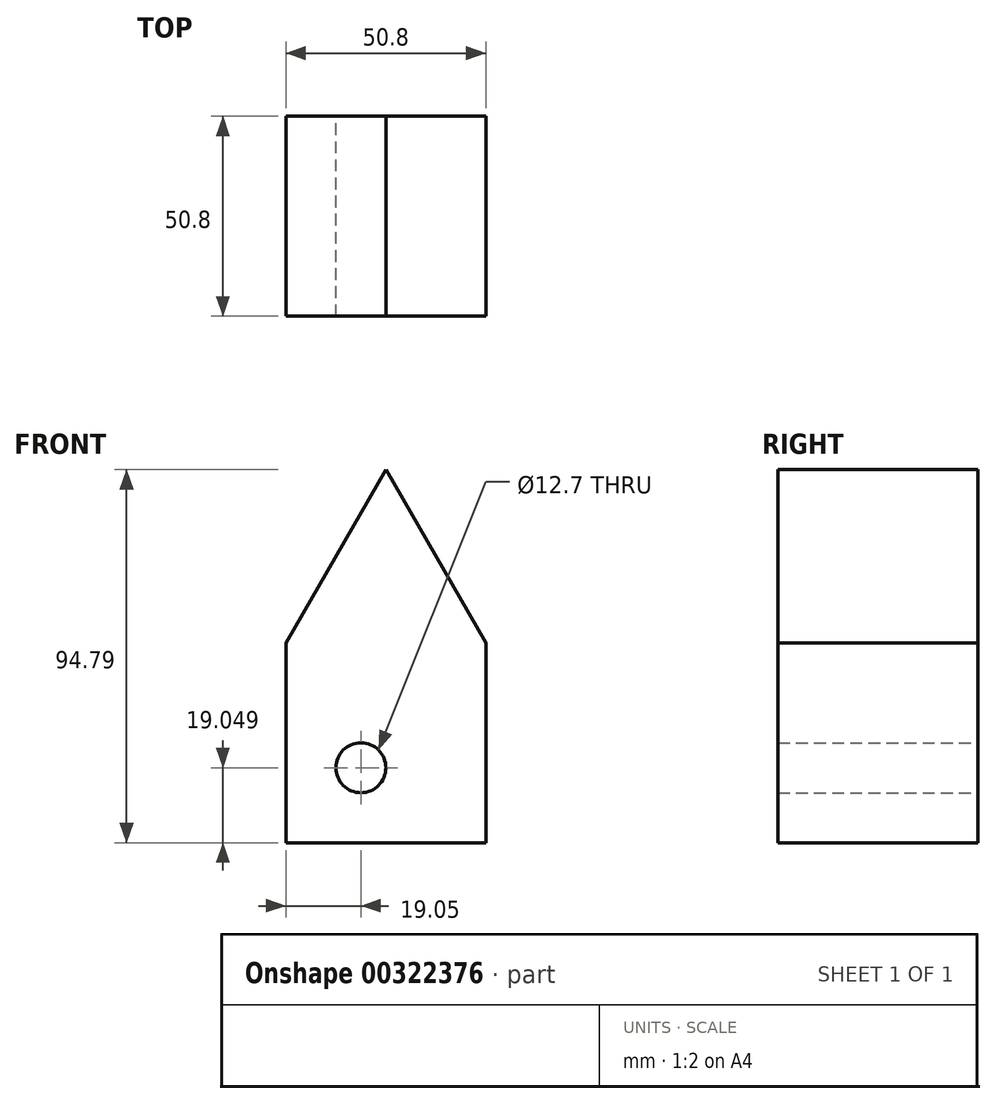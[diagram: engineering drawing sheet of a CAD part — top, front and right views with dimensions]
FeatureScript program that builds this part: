
annotation { "Feature Type Name" : "Feature", "Feature Type Description" : "" }
export const myFeature = defineFeature(function(context is Context, id is Id, definition is map)
    precondition{}
    {
        {
            var Q0;
            Q0=qCreatedBy(makeId("Front.planeOp"),FACE);
            var sketch = newSketch(context, id + "F0", { "sketchPlane" : qUnion([Q0])});
            skLineSegment(sketch, "E0.bottom", {"start": v(25.4, -20.27) * mm, "end": v(-25.4, -20.27) * mm});
            skLineSegment(sketch, "E0.left", {"start": v(25.4, -20.27) * mm, "end": v(25.4, 30.53) * mm});
            skLineSegment(sketch, "E0.right", {"start": v(-25.4, -20.27) * mm, "end": v(-25.4, 30.53) * mm});
            skLineSegment(sketch, "E1", {"start": v(-25.4, 30.53) * mm, "end": v(0, 74.52) * mm});
            skLineSegment(sketch, "E2", {"start": v(25.4, 30.53) * mm, "end": v(0, 74.52) * mm});
            skLineSegment(sketch, "E3.bottom", {"start": v(-25.4, -20.27) * mm, "end": v(-6.35, -20.27) * mm});
            skLineSegment(sketch, "E3.left", {"start": v(-25.4, -20.27) * mm, "end": v(-25.4, -1.22) * mm});
            skCircle(sketch, "E4", {"center": v(-6.35, -1.22) * mm, "radius": 6.35 * mm});
            skSolve(sketch);
        }
        {
            var Q0;
            Q0=makeQuery(id+"F0.imprint","IMPRINT",FACE,{"disambiguationData":[TD([[makeQuery(id+"F0.imprint","IMPRINT",EDGE,{"derivedFrom":sQuery(id+"F0.wireOp",EDGE,"E0.bottom")}),-1.0]])]});
            extrude(context, id + "F1", {"entities" : qUnion([Q0]), "depth" : 50.8 * mm});
        }
    });
